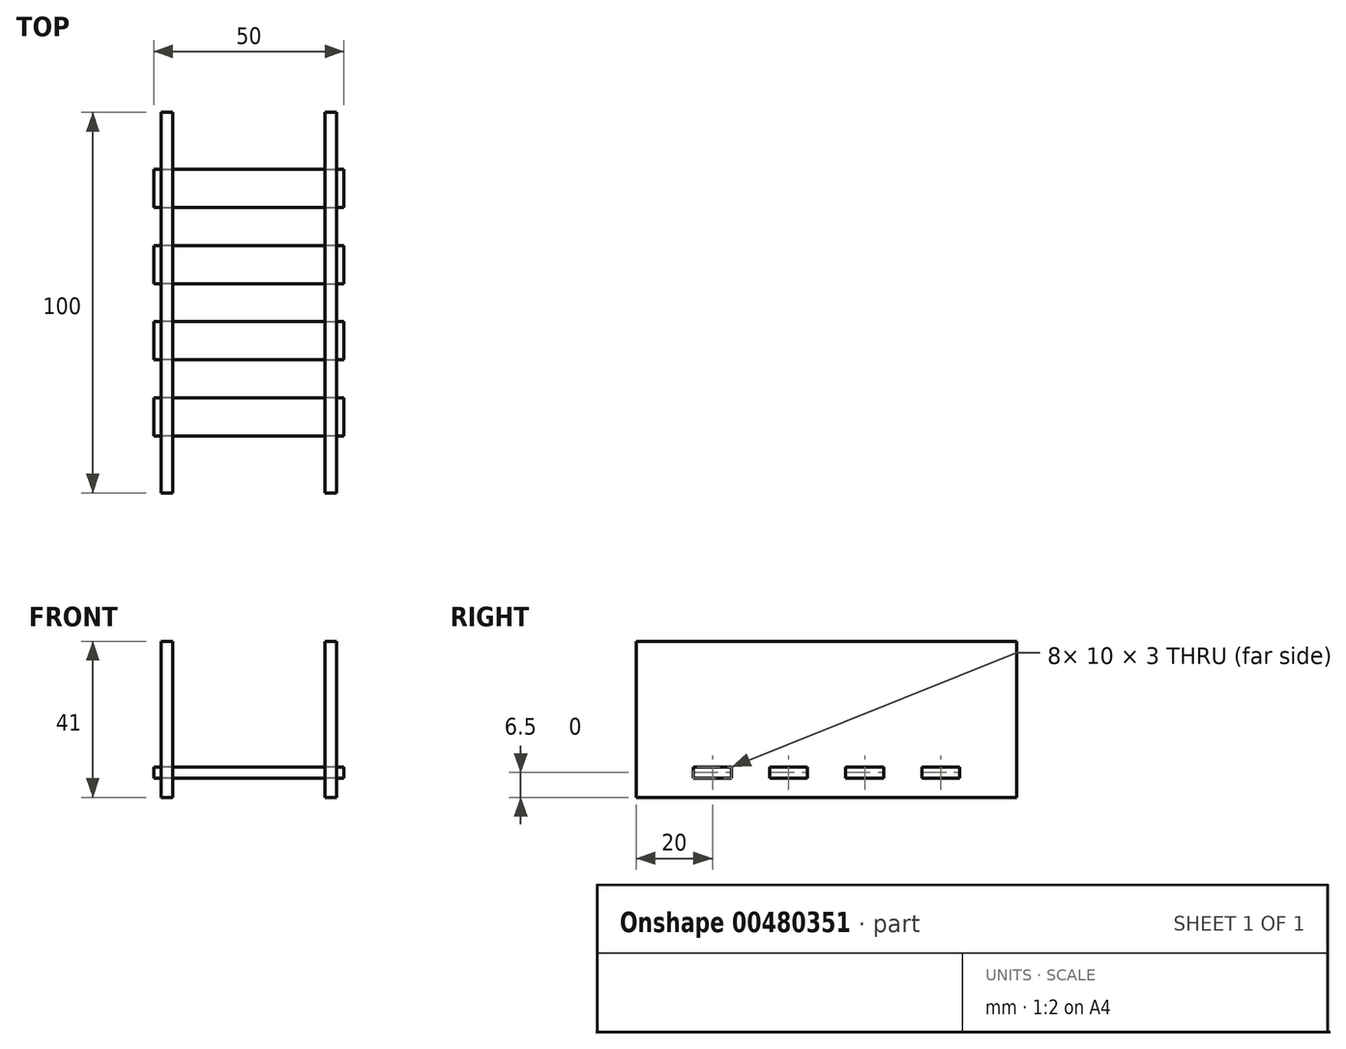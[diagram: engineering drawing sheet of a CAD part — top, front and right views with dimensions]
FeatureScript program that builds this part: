
annotation { "Feature Type Name" : "Feature", "Feature Type Description" : "" }
export const myFeature = defineFeature(function(context is Context, id is Id, definition is map)
    precondition{}
    {
        {
            assignVariable(context, id + "F0", {"name" : "botPlateWidth", "anyValue" : 40});
        }
        {
            assignVariable(context, id + "F1", {"name" : "plateThickness", "anyValue" : 3});
        }
        {
            var Q0;
            Q0=qCreatedBy(makeId("Top.planeOp"),FACE);
            var sketch = newSketch(context, id + "F2", { "sketchPlane" : qUnion([Q0])});
            skLineSegment(sketch, "E0.bottom", {"start": v(20, -45) * mm, "end": v(-20, -45) * mm});
            skLineSegment(sketch, "E0.top", {"start": v(20, 45) * mm, "end": v(-20, 45) * mm});
            skLineSegment(sketch, "E0.left", {"start": v(20, -45) * mm, "end": v(20, 45) * mm});
            skLineSegment(sketch, "E0.right", {"start": v(-20, -45) * mm, "end": v(-20, 45) * mm});
            skPoint(sketch, "E0.middle", {"position": v(0, 0) * mm});
            skLineSegment(sketch, "E1", {"start": v(-20, 45) * mm, "end": v(-20, 35) * mm});
            skLineSegment(sketch, "E2", {"start": v(-20, 35) * mm, "end": v(-20, 25) * mm});
            skLineSegment(sketch, "E3", {"start": v(-20, 25) * mm, "end": v(-20, 15) * mm});
            skLineSegment(sketch, "E4", {"start": v(-20, 15) * mm, "end": v(-20, 5) * mm});
            skLineSegment(sketch, "E5", {"start": v(-20, 5) * mm, "end": v(-20, -5) * mm});
            skLineSegment(sketch, "E6", {"start": v(-20, -5) * mm, "end": v(-20, -15) * mm});
            skLineSegment(sketch, "E7", {"start": v(-20, -15) * mm, "end": v(-20, -25) * mm});
            skLineSegment(sketch, "E8", {"start": v(-20, -25) * mm, "end": v(-20, -35) * mm});
            skLineSegment(sketch, "E9.bottom", {"start": v(-20, 35) * mm, "end": v(-25, 35) * mm});
            skLineSegment(sketch, "E9.top", {"start": v(-20, 25) * mm, "end": v(-25, 25) * mm});
            skLineSegment(sketch, "E9.right", {"start": v(-25, 35) * mm, "end": v(-25, 25) * mm});
            skLineSegment(sketch, "E10.bottom", {"start": v(-20, 15) * mm, "end": v(-25, 15) * mm});
            skLineSegment(sketch, "E10.top", {"start": v(-20, 5) * mm, "end": v(-25, 5) * mm});
            skLineSegment(sketch, "E10.right", {"start": v(-25, 15) * mm, "end": v(-25, 5) * mm});
            skLineSegment(sketch, "E11.bottom", {"start": v(-20, -5) * mm, "end": v(-25, -5) * mm});
            skLineSegment(sketch, "E11.top", {"start": v(-20, -15) * mm, "end": v(-25, -15) * mm});
            skLineSegment(sketch, "E11.right", {"start": v(-25, -5) * mm, "end": v(-25, -15) * mm});
            skLineSegment(sketch, "E12.bottom", {"start": v(-20, -25) * mm, "end": v(-25, -25) * mm});
            skLineSegment(sketch, "E12.top", {"start": v(-20, -35) * mm, "end": v(-25, -35) * mm});
            skLineSegment(sketch, "E12.right", {"start": v(-25, -25) * mm, "end": v(-25, -35) * mm});
            skLineSegment(sketch, "E13.bottom", {"start": v(20, -35) * mm, "end": v(25, -35) * mm});
            skLineSegment(sketch, "E13.top", {"start": v(20, -25) * mm, "end": v(25, -25) * mm});
            skLineSegment(sketch, "E13.left", {"start": v(20, -35) * mm, "end": v(20, -25) * mm});
            skLineSegment(sketch, "E13.right", {"start": v(25, -35) * mm, "end": v(25, -25) * mm});
            skLineSegment(sketch, "E14.bottom", {"start": v(20, -15) * mm, "end": v(25, -15) * mm});
            skLineSegment(sketch, "E14.top", {"start": v(20, -5) * mm, "end": v(25, -5) * mm});
            skLineSegment(sketch, "E14.left", {"start": v(20, -15) * mm, "end": v(20, -5) * mm});
            skLineSegment(sketch, "E14.right", {"start": v(25, -15) * mm, "end": v(25, -5) * mm});
            skLineSegment(sketch, "E15.bottom", {"start": v(20, 5) * mm, "end": v(25, 5) * mm});
            skLineSegment(sketch, "E15.top", {"start": v(20, 15) * mm, "end": v(25, 15) * mm});
            skLineSegment(sketch, "E15.left", {"start": v(20, 5) * mm, "end": v(20, 15) * mm});
            skLineSegment(sketch, "E15.right", {"start": v(25, 5) * mm, "end": v(25, 15) * mm});
            skLineSegment(sketch, "E16.bottom", {"start": v(20, 25) * mm, "end": v(25, 25) * mm});
            skLineSegment(sketch, "E16.top", {"start": v(20, 35) * mm, "end": v(25, 35) * mm});
            skLineSegment(sketch, "E16.left", {"start": v(20, 25) * mm, "end": v(20, 35) * mm});
            skLineSegment(sketch, "E16.right", {"start": v(25, 25) * mm, "end": v(25, 35) * mm});
            skSolve(sketch);
        }
        {
            var Q0;
            {var subQ6=sQuery(id+"F2.wireOp",EDGE,"E0.bottom");Q0=makeQuery(id+"F2.imprint","IMPRINT",FACE,{"disambiguationData":[TD([[makeQuery(id+"F2.imprint","IMPRINT",EDGE,{"derivedFrom":subQ6}),-1.0]])]});}
            var Q1;
            Q1=makeQuery(id+"F2.imprint","IMPRINT",FACE,{"disambiguationData":[TD([[makeQuery(id+"F2.imprint","IMPRINT",EDGE,{"derivedFrom":sQuery(id+"F2.wireOp",EDGE,"E10.bottom")}),1.0]])]});
            var Q2;
            Q2=makeQuery(id+"F2.imprint","IMPRINT",FACE,{"disambiguationData":[TD([[makeQuery(id+"F2.imprint","IMPRINT",EDGE,{"derivedFrom":sQuery(id+"F2.wireOp",EDGE,"E11.bottom")}),1.0]])]});
            var Q3;
            Q3=makeQuery(id+"F2.imprint","IMPRINT",FACE,{"disambiguationData":[TD([[makeQuery(id+"F2.imprint","IMPRINT",EDGE,{"derivedFrom":sQuery(id+"F2.wireOp",EDGE,"E12.bottom")}),1.0]])]});
            var Q4;
            Q4=makeQuery(id+"F2.imprint","IMPRINT",FACE,{"disambiguationData":[TD([[makeQuery(id+"F2.imprint","IMPRINT",EDGE,{"derivedFrom":sQuery(id+"F2.wireOp",EDGE,"E9.bottom")}),1.0]])]});
            var Q5;
            Q5=makeQuery(id+"F2.imprint","IMPRINT",FACE,{"disambiguationData":[TD([[makeQuery(id+"F2.imprint","IMPRINT",EDGE,{"derivedFrom":sQuery(id+"F2.wireOp",EDGE,"E16.bottom")}),1.0]])]});
            var Q6;
            Q6=makeQuery(id+"F2.imprint","IMPRINT",FACE,{"disambiguationData":[TD([[makeQuery(id+"F2.imprint","IMPRINT",EDGE,{"derivedFrom":sQuery(id+"F2.wireOp",EDGE,"E15.bottom")}),1.0]])]});
            var Q7;
            Q7=makeQuery(id+"F2.imprint","IMPRINT",FACE,{"disambiguationData":[TD([[makeQuery(id+"F2.imprint","IMPRINT",EDGE,{"derivedFrom":sQuery(id+"F2.wireOp",EDGE,"E14.bottom")}),1.0]])]});
            var Q8;
            Q8=makeQuery(id+"F2.imprint","IMPRINT",FACE,{"disambiguationData":[TD([[makeQuery(id+"F2.imprint","IMPRINT",EDGE,{"derivedFrom":sQuery(id+"F2.wireOp",EDGE,"E13.bottom")}),1.0]])]});
            extrude(context, id + "F3", {"entities" : qUnion([Q0, Q1, Q2, Q3, Q4, Q5, Q6, Q7, Q8]), "oppositeDirection" : true, "depth" : (getVariable(context, 'plateThickness')) * mm});
        }
        {
            var Q0;
            Q0=qCreatedBy(makeId("Right.planeOp"),FACE);
            var sketch = newSketch(context, id + "F4", { "sketchPlane" : qUnion([Q0])});
            skLineSegment(sketch, "E17", {"start": v(0, 0) * mm, "end": v(-45, 0) * mm, "construction": true});
            skLineSegment(sketch, "E18", {"start": v(0, 0) * mm, "end": v(45, 0) * mm, "construction": true});
            skLineSegment(sketch, "E19", {"start": v(-45, 0) * mm, "end": v(-35, 0) * mm, "construction": true});
            skLineSegment(sketch, "E20.bottom", {"start": v(-35, 0) * mm, "end": v(-25, 0) * mm});
            skLineSegment(sketch, "E20.top", {"start": v(-35, -3) * mm, "end": v(-25, -3) * mm});
            skLineSegment(sketch, "E20.left", {"start": v(-35, 0) * mm, "end": v(-35, -3) * mm});
            skLineSegment(sketch, "E20.right", {"start": v(-25, 0) * mm, "end": v(-25, -3) * mm});
            skLineSegment(sketch, "E21", {"start": v(-25, 0) * mm, "end": v(-15, 0) * mm, "construction": true});
            skLineSegment(sketch, "E22.bottom", {"start": v(-15, 0) * mm, "end": v(-5, 0) * mm});
            skLineSegment(sketch, "E22.top", {"start": v(-15, -3) * mm, "end": v(-5, -3) * mm});
            skLineSegment(sketch, "E22.left", {"start": v(-15, 0) * mm, "end": v(-15, -3) * mm});
            skLineSegment(sketch, "E22.right", {"start": v(-5, 0) * mm, "end": v(-5, -3) * mm});
            skLineSegment(sketch, "E23", {"start": v(-5, 0) * mm, "end": v(5, 0) * mm, "construction": true});
            skLineSegment(sketch, "E24.bottom", {"start": v(5, 0) * mm, "end": v(15, 0) * mm});
            skLineSegment(sketch, "E24.top", {"start": v(5, -3) * mm, "end": v(15, -3) * mm});
            skLineSegment(sketch, "E24.left", {"start": v(5, 0) * mm, "end": v(5, -3) * mm});
            skLineSegment(sketch, "E24.right", {"start": v(15, 0) * mm, "end": v(15, -3) * mm});
            skLineSegment(sketch, "E25", {"start": v(15, 0) * mm, "end": v(25, 0) * mm, "construction": true});
            skLineSegment(sketch, "E26.bottom", {"start": v(25, 0) * mm, "end": v(35, 0) * mm});
            skLineSegment(sketch, "E26.top", {"start": v(25, -3) * mm, "end": v(35, -3) * mm});
            skLineSegment(sketch, "E26.left", {"start": v(25, 0) * mm, "end": v(25, -3) * mm});
            skLineSegment(sketch, "E26.right", {"start": v(35, 0) * mm, "end": v(35, -3) * mm});
            skLineSegment(sketch, "E27", {"start": v(45, 0) * mm, "end": v(50, 0) * mm});
            skLineSegment(sketch, "E28", {"start": v(50, 0) * mm, "end": v(50, -8) * mm});
            skLineSegment(sketch, "E29", {"start": v(50, -8) * mm, "end": v(-50, -8) * mm});
            skLineSegment(sketch, "E30", {"start": v(-50, -8) * mm, "end": v(-50, 33) * mm});
            skLineSegment(sketch, "E31", {"start": v(-50, 33) * mm, "end": v(50, 33) * mm});
            skLineSegment(sketch, "E32", {"start": v(50, 33) * mm, "end": v(50, 0) * mm});
            skSolve(sketch);
        }
        {
            var Q0;
            Q0=makeQuery(id+"F4.imprint","IMPRINT",FACE,{"disambiguationData":[TD([[makeQuery(id+"F4.imprint","IMPRINT",EDGE,{"derivedFrom":sQuery(id+"F4.wireOp",EDGE,"E20.bottom")}),1.0]])]});
            extrude(context, id + "F5", {"entities" : qUnion([Q0]), "endBound" : BoundingType.SYMMETRIC, "depth" : (getVariable(context, 'botPlateWidth') + 2 * getVariable(context, 'plateThickness')) * mm});
        }
        {
            var Q0;
            Q0=makeQuery(id+"F4.imprint","IMPRINT",FACE,{"disambiguationData":[TD([[makeQuery(id+"F4.imprint","IMPRINT",EDGE,{"derivedFrom":sQuery(id+"F4.wireOp",EDGE,"E20.bottom")}),1.0]])]});
            extrude(context, id + "F6", {"entities" : qUnion([Q0]), "operationType" : NewBodyOperationType.REMOVE, "endBound" : BoundingType.SYMMETRIC, "oppositeDirection" : true, "depth" : (getVariable(context, 'botPlateWidth')) * mm});
        }
    });
